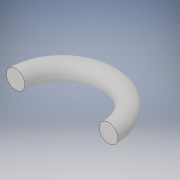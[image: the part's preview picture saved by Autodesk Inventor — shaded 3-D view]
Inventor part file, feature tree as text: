
AUTODESK INVENTOR PART (.ipt)
format: ipt  version: 2017 (Build 210142000, 142)  size: 138,752 bytes
history: native  units: in
note: dims shown in document units (in); Inventor stores cm internally (conversion verified against a paired STEP export)
features: sketch x2, sweep x1
ambient origin geometry x8: Origin, YZ Plane, XZ Plane, XY Plane, X Axis, Y Axis, Z Axis, Center Point
bodies: Solid1 (feature_tree)
feature tree (3):
  sweep  "Sweep1"
  sketch  "Sketch3"  dims[d2=3.0in d3=3.0in]
  sketch  "Sketch4"  dims[d4=15.0in d6=15.0in d7=0.0in d8=0.0in]
